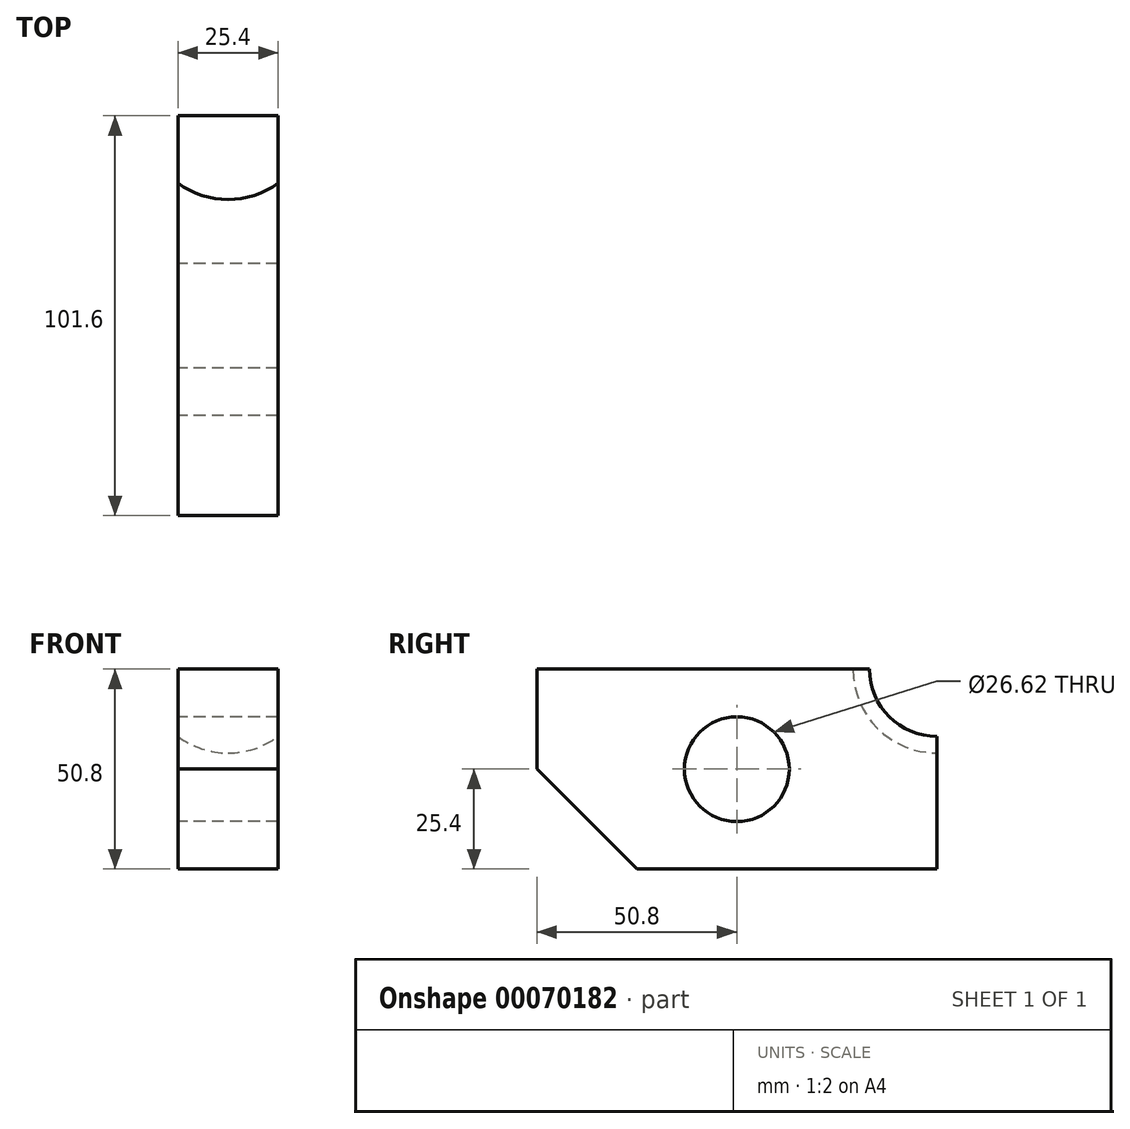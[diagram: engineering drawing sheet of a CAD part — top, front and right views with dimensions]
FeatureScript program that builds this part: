
annotation { "Feature Type Name" : "Feature", "Feature Type Description" : "" }
export const myFeature = defineFeature(function(context is Context, id is Id, definition is map)
    precondition{}
    {
        {
            var Q0;
            Q0=qCreatedBy(makeId("Right.planeOp"),FACE);
            var sketch = newSketch(context, id + "F0", { "sketchPlane" : qUnion([Q0])});
            skLineSegment(sketch, "E0.rect.bottom", {"start": v(50.8, -25.4) * mm, "end": v(-50.8, -25.4) * mm});
            skLineSegment(sketch, "E0.rect.top", {"start": v(50.8, 25.4) * mm, "end": v(-50.8, 25.4) * mm});
            skLineSegment(sketch, "E0.rect.left", {"start": v(50.8, -25.4) * mm, "end": v(50.8, 25.4) * mm});
            skLineSegment(sketch, "E0.rect.right", {"start": v(-50.8, -25.4) * mm, "end": v(-50.8, 25.4) * mm});
            skPoint(sketch, "E0.rect.middle", {"position": v(0, 0) * mm});
            skArc(sketch, "E1", {"start": v(50.8, 4.1) * mm, "mid": v(72.1, 25.4) * mm, "end": v(50.8, 46.7) * mm});
            skLineSegment(sketch, "E2", {"start": v(50.8, 46.7) * mm, "end": v(50.8, 25.4) * mm});
            skCircle(sketch, "E3", {"center": v(0, 0) * mm, "radius": 13.3 * mm});
            skCircle(sketch, "E4", {"center": v(0, 0) * mm, "radius": 9.1 * mm});
            skSolve(sketch);
        }
        {
            var Q0;
            {var subQ3=sQuery(id+"F0.wireOp",EDGE,"E0.rect.bottom");Q0=makeQuery(id+"F0.imprint","IMPRINT",FACE,{"disambiguationData":[TD([[makeQuery(id+"F0.imprint","IMPRINT",EDGE,{"derivedFrom":subQ3}),-1.0]])]});}
            extrude(context, id + "F1", {"entities" : qUnion([Q0]), "endBound" : BoundingType.SYMMETRIC, "depth" : 25.4 * mm});
        }
        {
            var Q0;
            {var subQ0=sQuery(id+"F0.wireOp",EDGE,"E0.rect.left");var subQ4=sQuery(id+"F0.wireOp",EDGE,"E0.rect.bottom");var subQ5=makeQuery(id+"F0.imprint","INTERSECT",VERTEX,{"derivedFrom":[subQ4,subQ0]});Q0=makeQuery(id+"F0.imprint","IMPRINT",FACE,{"disambiguationData":[TD([[makeQuery(id+"F0.imprint","IMPRINT",EDGE,{"disambiguationData":[TD([[subQ5,-1.0]])],"derivedFrom":subQ4}),-1.0]])]});}
            extrude(context, id + "F2", {"entities" : qUnion([Q0]), "endBound" : BoundingType.SYMMETRIC, "depth" : 25.4 * mm});
        }
        {
            var Q0;
            {var subQ2=sQuery(id+"F0.wireOp",EDGE,"E1");Q0=makeQuery(id+"F0.imprint","IMPRINT",FACE,{"disambiguationData":[TD([[makeQuery(id+"F0.imprint","IMPRINT",EDGE,{"derivedFrom":subQ2}),1.0]])]});}
            var Q1;
            Q1=sQuery(id+"F0.wireOp",EDGE,"E2");
            revolve(context, id + "F3", {"operationType" : NewBodyOperationType.ADD, "entities" : qUnion([Q0]), "axis" : qUnion([Q1]), "revolveType" : RevolveType.FULL});
        }
        {
            var Q0;
            Q0=makeQuery(id+"F1.opExtrude","SWEPT_EDGE",EDGE,{"disambiguationData":[OSD([sQuery(id+"F0.wireOp",EDGE,"E0.rect.bottom"),sQuery(id+"F0.wireOp",EDGE,"E0.rect.right")])]});
            chamfer(context, id + "F4", {"entities" : qUnion([Q0]), "width" : 25.4 * mm, "tangentPropagation" : true});
        }
    });
